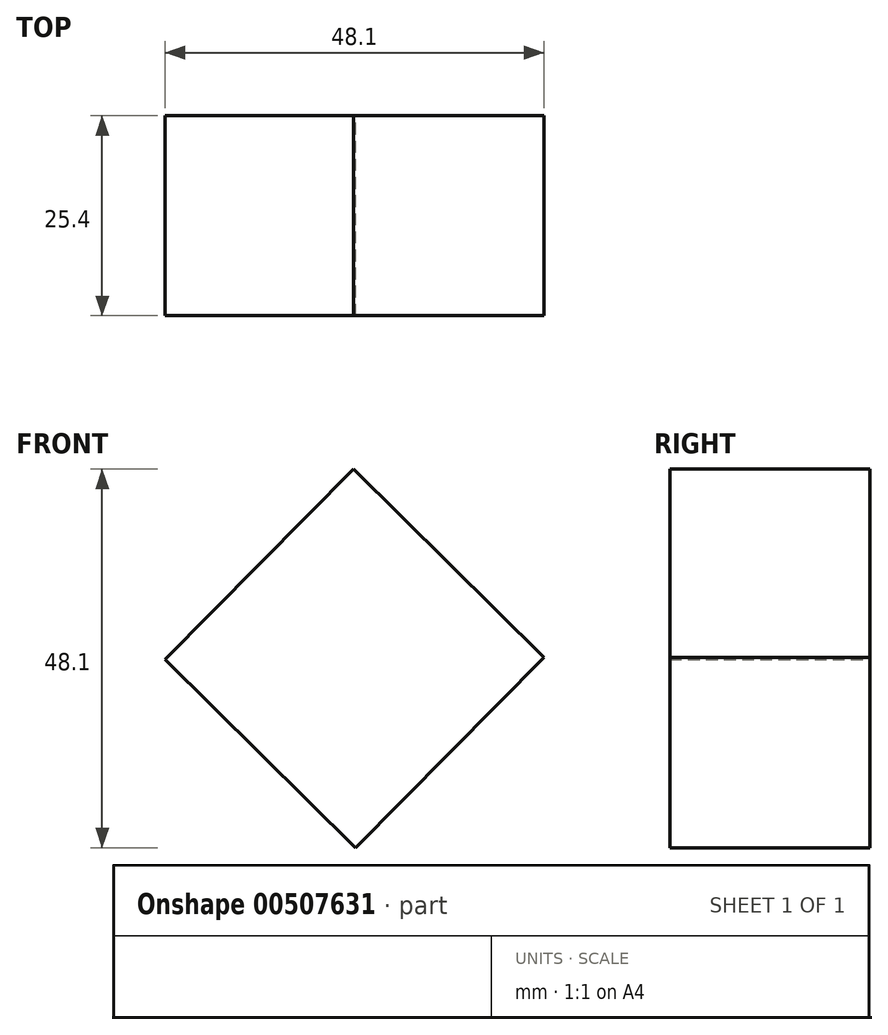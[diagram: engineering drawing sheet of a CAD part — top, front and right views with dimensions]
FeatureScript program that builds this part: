
annotation { "Feature Type Name" : "Feature", "Feature Type Description" : "" }
export const myFeature = defineFeature(function(context is Context, id is Id, definition is map)
    precondition{}
    {
        {
            var Q0;
            Q0=qCreatedBy(makeId("Front.planeOp"),FACE);
            var sketch = newSketch(context, id + "F0", { "sketchPlane" : qUnion([Q0])});
            skCircle(sketch, "E0.cCircle", {"center": v(0, 0) * mm, "radius": 17 * mm, "construction": true});
            skLineSegment(sketch, "E0.0", {"start": v(0.15, -24.05) * mm, "end": v(-24.05, -0.15) * mm});
            skLineSegment(sketch, "E0.1", {"start": v(-24.05, -0.15) * mm, "end": v(-0.15, 24.05) * mm});
            skLineSegment(sketch, "E0.2", {"start": v(-0.15, 24.05) * mm, "end": v(24.05, 0.15) * mm});
            skLineSegment(sketch, "E0.3", {"start": v(24.05, 0.15) * mm, "end": v(0.15, -24.05) * mm});
            skPoint(sketch, "E0.0.midPoint", {"position": v(-11.95, -12.1) * mm});
            skSolve(sketch);
        }
        {
            var Q0;
            Q0=makeQuery(id+"F0.imprint","IMPRINT",FACE,{"disambiguationData":[TD([[makeQuery(id+"F0.imprint","IMPRINT",EDGE,{"derivedFrom":sQuery(id+"F0.wireOp",EDGE,"E0.0")}),-1.0]])]});
            extrude(context, id + "F1", {"entities" : qUnion([Q0]), "endBound" : BoundingType.SYMMETRIC, "depth" : 25.4 * mm});
        }
    });
